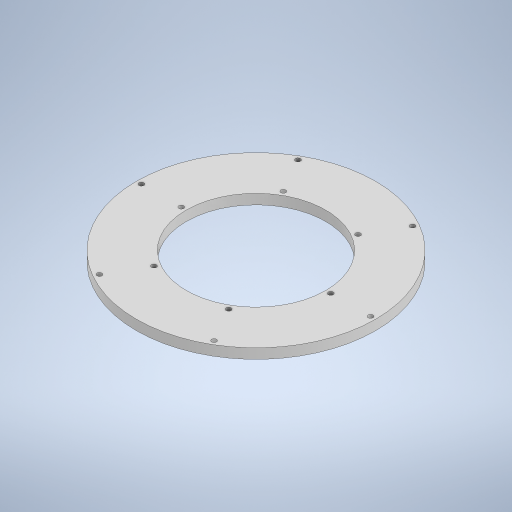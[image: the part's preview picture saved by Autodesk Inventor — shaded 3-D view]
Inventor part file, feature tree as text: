
AUTODESK INVENTOR PART (.ipt)
format: ipt  version: 2023 (Build 270158000, 158)  size: 292,864 bytes
history: native  units: in
note: dims shown in document units (in); Inventor stores cm internally (conversion verified against a paired STEP export)
features: extrude x1, sketch x1
ambient origin geometry x8: Origin, YZ Plane, XZ Plane, XY Plane, X Axis, Y Axis, Z Axis, Center Point
bodies: Solid1 (feature_tree)
feature tree (2):
  extrude  "Extrusion1"  Depth=0.5in
  sketch  "Sketch1"  dims[d0=20.0in d1=1.0in d2=45.0deg d3=0.0in d4=0.0in d5=45.0deg d6=0.5in d7=0.5in d8=0.5in d9=0.5in d10=12.0in d11=8.0in d12=7.0in d13=0.5in d14=0.25in d15=5.75in d16=2.3622in d18=360.0deg d20=0.25in d21=3.75in d22=2.3622in d24=360.0deg d26=0.2in d27=0.5in d28=0.0in]
